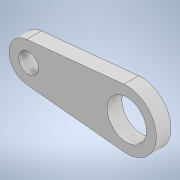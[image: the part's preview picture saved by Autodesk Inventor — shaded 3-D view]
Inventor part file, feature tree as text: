
AUTODESK INVENTOR PART (.ipt)
format: ipt  version: 2022 (Build 260153000, 153)  size: 110,080 bytes
history: native  units: mm
features: other x1, extrude x1, sketch x1
ambient origin geometry x8: Origin, YZ Plane, XZ Plane, XY Plane, X Axis, Y Axis, Z Axis, Center Point
bodies: Body1 (feature_tree)
feature tree (3):
  other  "Sólido1"
  extrude  "Extrusão1"  Depth=15.0mm
  sketch  "Esboço1"  dims[d0=20.0mm d1=40.0mm d2=40.0mm d3=60.0mm d4=100.0mm d5=15.0mm d6=0.0mm]
